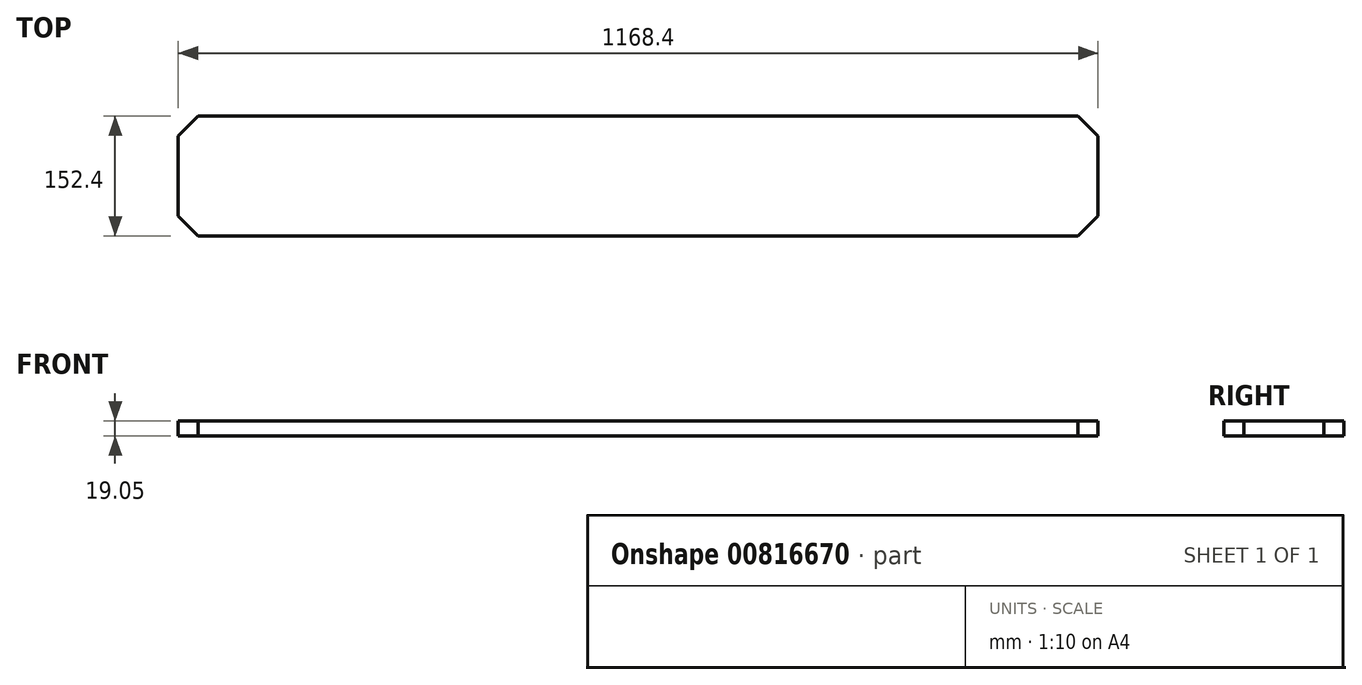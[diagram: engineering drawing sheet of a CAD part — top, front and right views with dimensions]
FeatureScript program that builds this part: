
annotation { "Feature Type Name" : "Feature", "Feature Type Description" : "" }
export const myFeature = defineFeature(function(context is Context, id is Id, definition is map)
    precondition{}
    {
        {
            var Q0;
            Q0=qCreatedBy(makeId("Top.planeOp"),FACE);
            var sketch = newSketch(context, id + "F0", { "sketchPlane" : qUnion([Q0])});
            skLineSegment(sketch, "E0.bottom", {"start": v(-658.75, 77.92) * mm, "end": v(509.65, 77.92) * mm});
            skLineSegment(sketch, "E0.top", {"start": v(-658.75, -74.48) * mm, "end": v(509.65, -74.48) * mm});
            skLineSegment(sketch, "E0.left", {"start": v(-658.75, 77.92) * mm, "end": v(-658.75, -74.48) * mm});
            skLineSegment(sketch, "E0.right", {"start": v(509.65, 77.92) * mm, "end": v(509.65, -74.48) * mm});
            skSolve(sketch);
        }
        {
            var Q0;
            Q0 = qSketchRegion(id + "F0", true);
            extrude(context, id + "F1", {"entities" : qUnion([Q0]), "oppositeDirection" : true, "depth" : 19.05 * mm, "offsetDistance" : 25.4 * mm});
        }
        {
            var Q0;
            Q0=makeQuery(id+"F1.opExtrude","SWEPT_EDGE",EDGE,{"disambiguationData":[OSD([sQuery(id+"F0.wireOp",EDGE,"E0.bottom"),sQuery(id+"F0.wireOp",EDGE,"E0.left")])]});
            var Q1;
            Q1=makeQuery(id+"F1.opExtrude","SWEPT_EDGE",EDGE,{"disambiguationData":[OSD([sQuery(id+"F0.wireOp",EDGE,"E0.top"),sQuery(id+"F0.wireOp",EDGE,"E0.left")])]});
            var Q2;
            Q2=makeQuery(id+"F1.opExtrude","SWEPT_EDGE",EDGE,{"disambiguationData":[OSD([sQuery(id+"F0.wireOp",EDGE,"E0.bottom"),sQuery(id+"F0.wireOp",EDGE,"E0.right")])]});
            var Q3;
            Q3=makeQuery(id+"F1.opExtrude","SWEPT_EDGE",EDGE,{"disambiguationData":[OSD([sQuery(id+"F0.wireOp",EDGE,"E0.top"),sQuery(id+"F0.wireOp",EDGE,"E0.right")])]});
            chamfer(context, id + "F2", {"entities" : qUnion([Q0, Q1, Q2, Q3]), "width" : 25.4 * mm, "tangentPropagation" : true});
        }
    });
